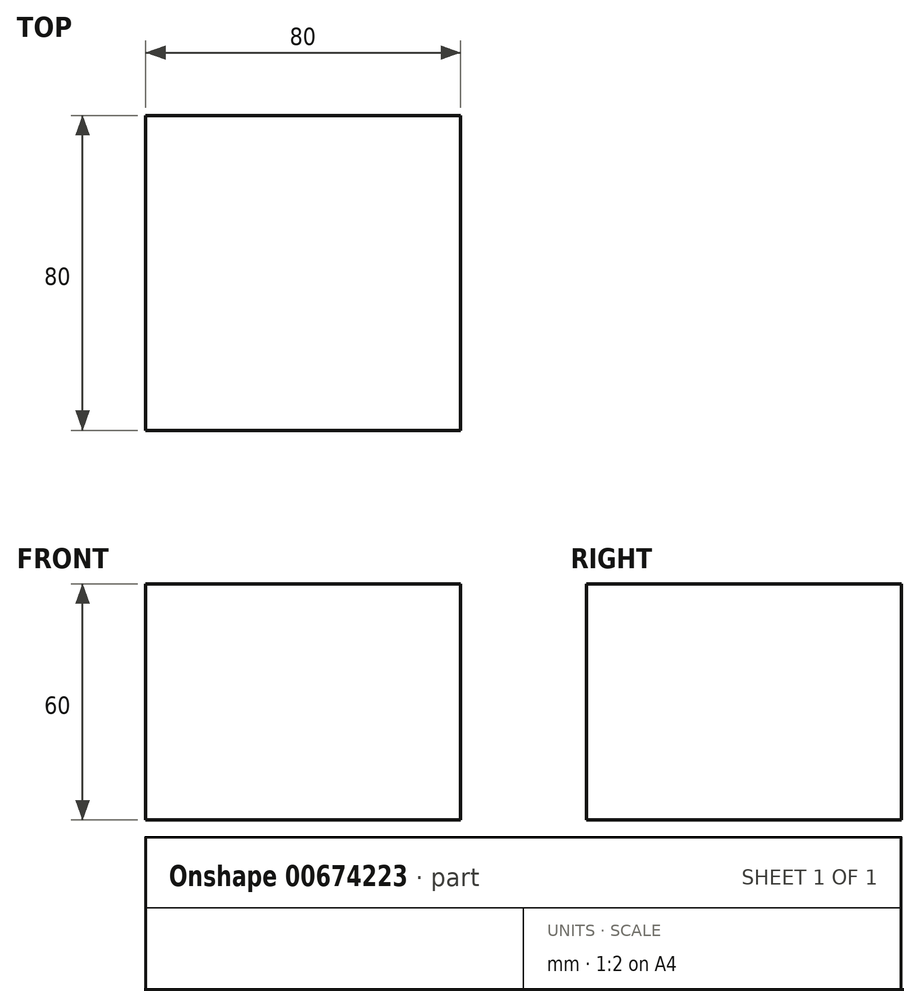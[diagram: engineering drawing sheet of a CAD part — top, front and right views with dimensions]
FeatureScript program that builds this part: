
annotation { "Feature Type Name" : "Feature", "Feature Type Description" : "" }
export const myFeature = defineFeature(function(context is Context, id is Id, definition is map)
    precondition{}
    {
        {
            var Q0;
            Q0=qCreatedBy(makeId("Front.planeOp"),FACE);
            var sketch = newSketch(context, id + "F0", { "sketchPlane" : qUnion([Q0])});
            skLineSegment(sketch, "E0.bottom", {"start": v(-80, 24.44) * mm, "end": v(0, 24.44) * mm});
            skLineSegment(sketch, "E0.top", {"start": v(-80, -35.56) * mm, "end": v(0, -35.56) * mm});
            skLineSegment(sketch, "E0.left", {"start": v(-80, 24.44) * mm, "end": v(-80, -35.56) * mm});
            skLineSegment(sketch, "E0.right", {"start": v(0, 24.44) * mm, "end": v(0, -35.56) * mm});
            skSolve(sketch);
        }
        {
            var Q0;
            Q0=makeQuery(id+"F0.imprint","IMPRINT",FACE,{"disambiguationData":[TD([[makeQuery(id+"F0.imprint","IMPRINT",EDGE,{"derivedFrom":sQuery(id+"F0.wireOp",EDGE,"E0.bottom")}),-1.0]])]});
            extrude(context, id + "F1", {"entities" : qUnion([Q0]), "depth" : 80 * mm, "offsetDistance" : 25 * mm});
        }
    });
